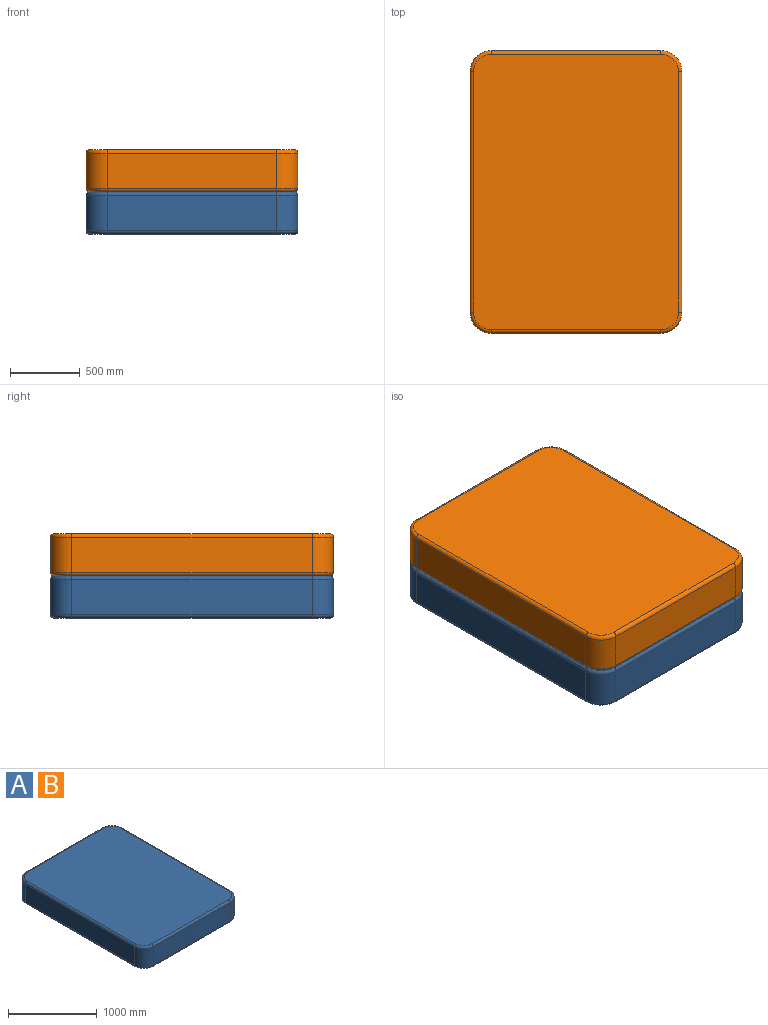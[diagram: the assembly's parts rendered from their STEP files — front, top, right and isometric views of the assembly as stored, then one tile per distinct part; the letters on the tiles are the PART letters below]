
ASSEMBLY  parts=2 mates=1
PART A: 26 faces, bbox 1549.1x2057.1x304.8 mm
  f0: plane 1727.2x254mm, normal (-1,0,0), area 438708.8mm2, adj f6,f9,f15,f24
  f1: plane 1219.2x254mm, normal (0,-1,0), area 309676.8mm2, adj f6,f7,f16,f23
  f2: plane 1727.2x254mm, normal (1,0,0), area 438708.8mm2, adj f7,f8,f12,f19
  f3: plane 1219.2x254mm, normal (0,1,0), area 309676.8mm2, adj f8,f9,f11,f20
  f4: plane 1981.2x1473.2mm, normal (0,0,1), area 2904858.6mm2, adj f10,f11,f12,f13,f14,f15,f16,f17
  f5: plane 1981.2x1473.2mm, normal (0,0,-1), area 2904858.6mm2, adj f18,f19,f20,f21,f22,f23,f24,f25
  f6: cylinder r=152.4mm len=254mm, axis (0,0,-1), area 60804.9mm2, adj f0,f1,f17,f25
  f7: cylinder r=152.4mm len=254mm, axis (0,0,1), area 60804.9mm2, adj f1,f2,f14,f21
  f8: cylinder r=152.4mm len=254mm, axis (0,0,-1), area 60804.9mm2, adj f2,f3,f10,f18
  f9: cylinder r=152.4mm len=254mm, axis (0,0,1), area 60804.9mm2, adj f0,f3,f13,f22
  f10: torus R=127mm, axis (0,0,1), area 8972.8mm2, adj f4,f8,f11,f12
  f11: cylinder r=25.4mm len=1219.2mm, axis (1,0,0), area 48643.9mm2, adj f3,f4,f10,f13
  f12: cylinder r=25.4mm len=1727.2mm, axis (0,-1,0), area 68912.2mm2, adj f2,f4,f10,f14
  f13: torus R=127mm, axis (0,0,1), area 8972.8mm2, adj f4,f9,f11,f15
  f14: torus R=127mm, axis (0,0,1), area 8972.8mm2, adj f4,f7,f12,f16
  f15: cylinder r=25.4mm len=1727.2mm, axis (0,1,0), area 68912.2mm2, adj f0,f4,f13,f17
  f16: cylinder r=25.4mm len=1219.2mm, axis (-1,0,0), area 48643.9mm2, adj f1,f4,f14,f17
  f17: torus R=127mm, axis (0,0,1), area 8972.8mm2, adj f4,f6,f15,f16
  f18: torus R=127mm, axis (0,0,1), area 8972.8mm2, adj f5,f8,f19,f20
  f19: cylinder r=25.4mm len=1727.2mm, axis (0,1,0), area 68912.2mm2, adj f2,f5,f18,f21
  f20: cylinder r=25.4mm len=1219.2mm, axis (-1,0,0), area 48643.9mm2, adj f3,f5,f18,f22
  f21: torus R=127mm, axis (0,0,1), area 8972.8mm2, adj f5,f7,f19,f23
  f22: torus R=127mm, axis (0,0,1), area 8972.8mm2, adj f5,f9,f20,f24
  f23: cylinder r=25.4mm len=1219.2mm, axis (1,0,0), area 48643.9mm2, adj f1,f5,f21,f25
  f24: cylinder r=25.4mm len=1727.2mm, axis (0,-1,0), area 68912.2mm2, adj f0,f5,f22,f25
  f25: torus R=127mm, axis (0,0,1), area 8972.8mm2, adj f5,f6,f23,f24
PART B: same geometry as A
PLACE A at identity fixed
PLACE B t=(0,0,304.8)mm
MATE fastened B.f5 <-> A.f4  axis (0,0,-1) through (0,0,304.8)mm
